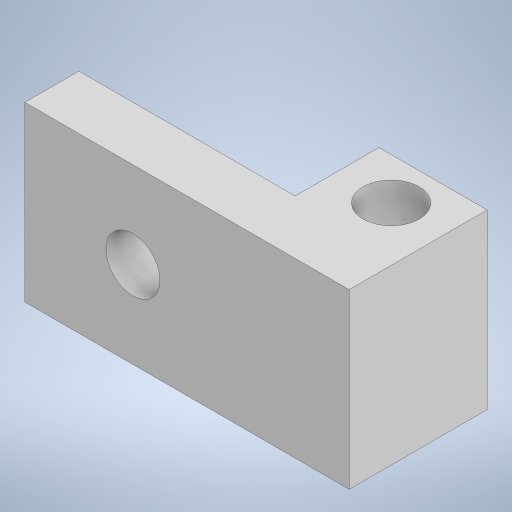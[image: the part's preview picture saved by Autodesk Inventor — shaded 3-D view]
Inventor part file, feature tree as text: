
AUTODESK INVENTOR PART (.ipt)
format: ipt  version: 2023 (Build 270158000, 158)  size: 219,136 bytes
history: native  units: in
note: dims shown in document units (in); Inventor stores cm internally (conversion verified against a paired STEP export)
features: extrude x4, sketch x4
ambient origin geometry x8: Origin, YZ Plane, XZ Plane, XY Plane, X Axis, Y Axis, Z Axis, Center Point
bodies: Solid1 (feature_tree)
feature tree (8):
  extrude  "Extrusion1"  Depth=0.6299in
  extrude  "Extrusion2"  Depth=0.3937in
  extrude  "Extrusion3"  Depth=0.1969in TaperAngle=0.0deg
  extrude  "Extrusion4"  Depth=0.3055in
  sketch  "Sketch1"  dims[d0=0.7874in d1=0.6299in]
  sketch  "Sketch2"  dims[d2=0.315in d3=0.3937in]
  sketch  "Sketch3"  dims[d4=0.1969in d5=0.1969in d6=0.0in]
  sketch  "Sketch4"  dims[d7=0.3937in d8=0.3055in d9=0.2047in d10=0.6299in d11=0.0in d12=0.3543in d13=0.0in d14=0.1969in d15=0.0in d16=0.2047in]
